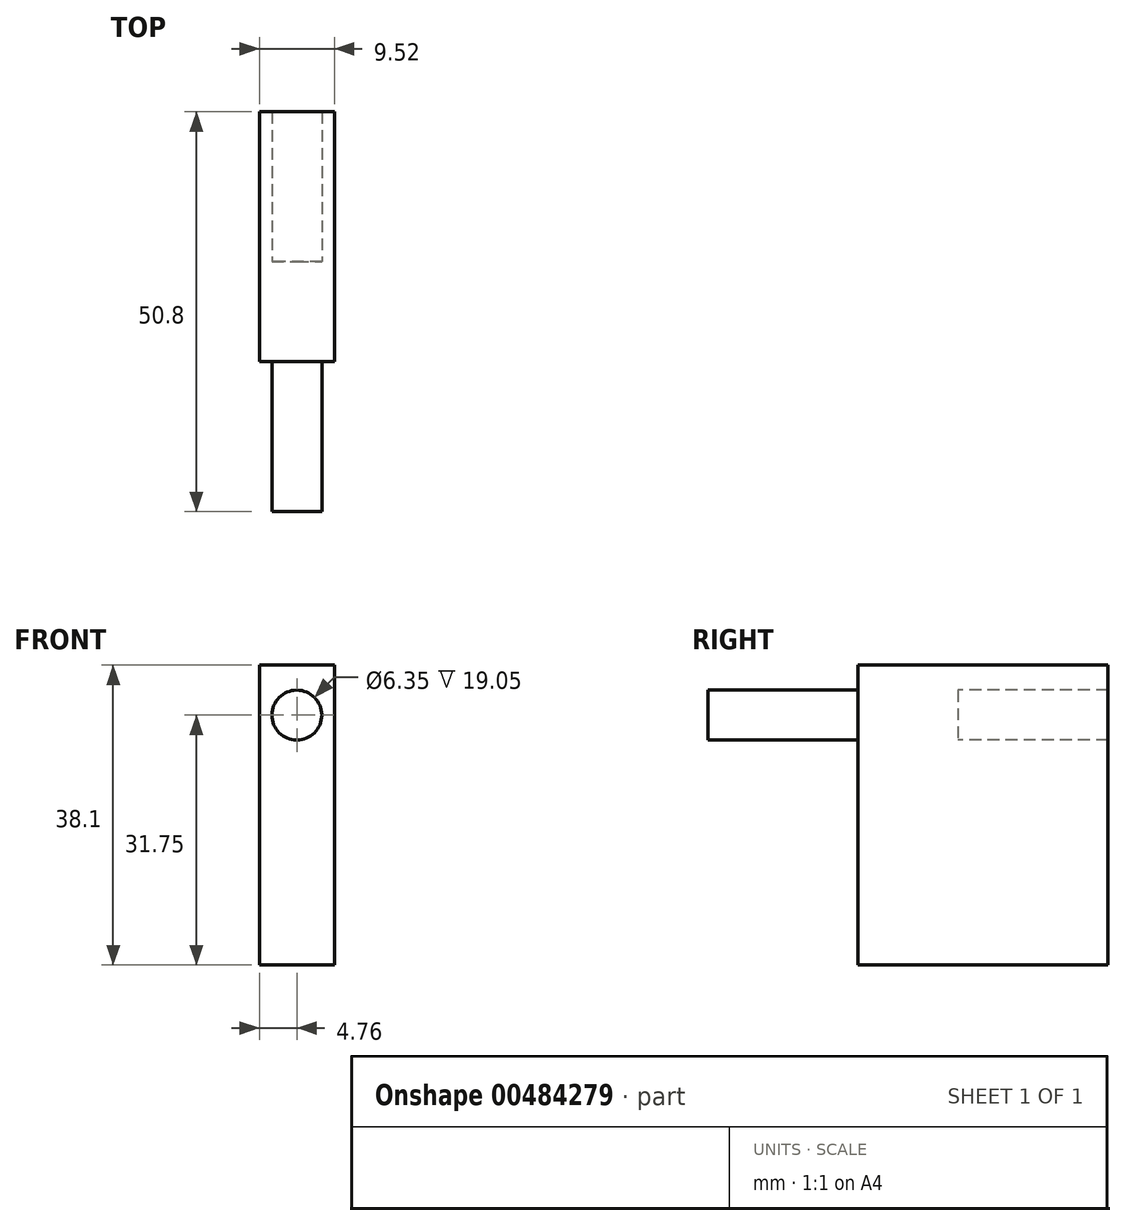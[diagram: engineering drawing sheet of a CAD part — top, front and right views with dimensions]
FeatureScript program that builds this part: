
annotation { "Feature Type Name" : "Feature", "Feature Type Description" : "" }
export const myFeature = defineFeature(function(context is Context, id is Id, definition is map)
    precondition{}
    {
        {
            var Q0;
            Q0=qCreatedBy(makeId("Front.planeOp"),FACE);
            var sketch = newSketch(context, id + "F0", { "sketchPlane" : qUnion([Q0])});
            skLineSegment(sketch, "E0.bottom", {"start": v(4.76, 19.05) * mm, "end": v(-4.76, 19.05) * mm});
            skLineSegment(sketch, "E0.top", {"start": v(4.76, -19.05) * mm, "end": v(-4.76, -19.05) * mm});
            skLineSegment(sketch, "E0.left", {"start": v(4.76, 19.05) * mm, "end": v(4.76, -19.05) * mm});
            skLineSegment(sketch, "E0.right", {"start": v(-4.76, 19.05) * mm, "end": v(-4.76, -19.05) * mm});
            skPoint(sketch, "E0.middle", {"position": v(0, 0) * mm});
            skCircle(sketch, "E1", {"center": v(0, 12.7) * mm, "radius": 2.38 * mm});
            skSolve(sketch);
        }
        {
            var Q0;
            Q0=makeQuery(id+"F0.imprint","IMPRINT",FACE,{"disambiguationData":[TD([[makeQuery(id+"F0.imprint","IMPRINT",EDGE,{"derivedFrom":sQuery(id+"F0.wireOp",EDGE,"E0.bottom")}),1.0]])]});
            extrude(context, id + "F1", {"entities" : qUnion([Q0]), "depth" : 12.7 * mm});
        }
        {
            var Q0;
            Q0=makeQuery(id+"F1.opExtrude","CAP_FACE",FACE,{"disambiguationData":[OSD([sQuery(id+"F0.wireOp",EDGE,"E0.bottom"),sQuery(id+"F0.wireOp",EDGE,"E0.top"),sQuery(id+"F0.wireOp",EDGE,"E0.left"),sQuery(id+"F0.wireOp",EDGE,"E0.right"),sQuery(id+"F0.wireOp",EDGE,"E1")])],"isStart":false});
            var sketch = newSketch(context, id + "F2", { "sketchPlane" : qUnion([Q0])});
            skCircle(sketch, "E2.0", {"center": v(0, 12.7) * mm, "radius": 2.38 * mm});
            skCircle(sketch, "E3", {"center": v(0, 12.7) * mm, "radius": 3.18 * mm});
            skSolve(sketch);
        }
        {
            var Q0;
            Q0=makeQuery(id+"F2.imprint","IMPRINT",FACE,{"disambiguationData":[TD([[makeQuery(id+"F2.imprint","IMPRINT",EDGE,{"derivedFrom":sQuery(id+"F2.wireOp",EDGE,"E2.0")}),1.0]])]});
            var Q1;
            Q1=sQuery(id+"F2.wireOp",EDGE,"E2.0");
            extrude(context, id + "F3", {"entities" : qUnion([Q0]), "surfaceEntities" : qUnion([Q1]), "oppositeDirection" : true, "depth" : 12.7 * mm});
        }
        {
            var Q0;
            Q0=makeQuery(id+"F2.imprint","IMPRINT",FACE,{"disambiguationData":[TD([[makeQuery(id+"F2.imprint","IMPRINT",EDGE,{"derivedFrom":sQuery(id+"F2.wireOp",EDGE,"E2.0")}),-1.0]])]});
            var Q1;
            Q1=makeQuery(id+"F2.imprint","IMPRINT",FACE,{"disambiguationData":[TD([[makeQuery(id+"F2.imprint","IMPRINT",EDGE,{"derivedFrom":sQuery(id+"F2.wireOp",EDGE,"E2.0")}),1.0]])]});
            var Q2;
            Q2=sQuery(id+"F2.wireOp",EDGE,"E3");
            extrude(context, id + "F4", {"entities" : qUnion([Q0, Q1]), "operationType" : NewBodyOperationType.ADD, "surfaceEntities" : qUnion([Q2]), "depth" : 19.05 * mm});
        }
        {
            var Q0;
            Q0=makeQuery(id+"F1.opExtrude","CAP_FACE",FACE,{"disambiguationData":[OSD([sQuery(id+"F0.wireOp",EDGE,"E0.bottom"),sQuery(id+"F0.wireOp",EDGE,"E0.top"),sQuery(id+"F0.wireOp",EDGE,"E0.left"),sQuery(id+"F0.wireOp",EDGE,"E0.right"),sQuery(id+"F0.wireOp",EDGE,"E1")])],"isStart":true});
            var sketch = newSketch(context, id + "F5", { "sketchPlane" : qUnion([Q0])});
            skCircle(sketch, "E4.0", {"center": v(0, 12.7) * mm, "radius": 3.18 * mm});
            skSolve(sketch);
        }
        {
            var Q0;
            Q0=makeQuery(id+"F5.imprint","IMPRINT",FACE,{"disambiguationData":[TD([[makeQuery(id+"F5.imprint","IMPRINT",EDGE,{"derivedFrom":makeQuery(id+"F1.opExtrude","CAP_EDGE",EDGE,{"disambiguationData":[OSD([sQuery(id+"F0.wireOp",EDGE,"E1")])],"isStart":true})}),-1.0]])]});
            var Q1;
            Q1=makeQuery(id+"F5.imprint","IMPRINT",FACE,{"disambiguationData":[TD([[makeQuery(id+"F5.imprint","IMPRINT",EDGE,{"derivedFrom":sQuery(id+"F5.wireOp",EDGE,"E4.0")}),-1.0]])]});
            var Q2;
            Q2=sQuery(id+"F5.wireOp",EDGE,"E4.0");
            extrude(context, id + "F6", {"entities" : qUnion([Q0, Q1]), "operationType" : NewBodyOperationType.ADD, "surfaceEntities" : qUnion([Q2]), "depth" : 19.05 * mm});
        }
    });
